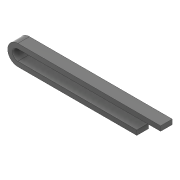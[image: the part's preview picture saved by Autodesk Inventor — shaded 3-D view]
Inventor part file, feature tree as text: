
AUTODESK INVENTOR PART (.ipt)
format: ipt  version: 2020 (Build 240168000, 168)  size: 100,352 bytes
history: native  units: mm
features: extrude x1, sketch x1
ambient origin geometry x8: Origin, YZ Plane, XZ Plane, XY Plane, X Axis, Y Axis, Z Axis, Center Point
bodies: Solid1 (feature_tree)
feature tree (2):
  extrude  "Extrusion1"  Depth=20.0mm
  sketch  "Sketch1"  dims[d0=85.0mm d1=20.0mm d2=20.0mm d4=500.0mm d5=49.0mm d6=0.0mm d9=600.0mm]
